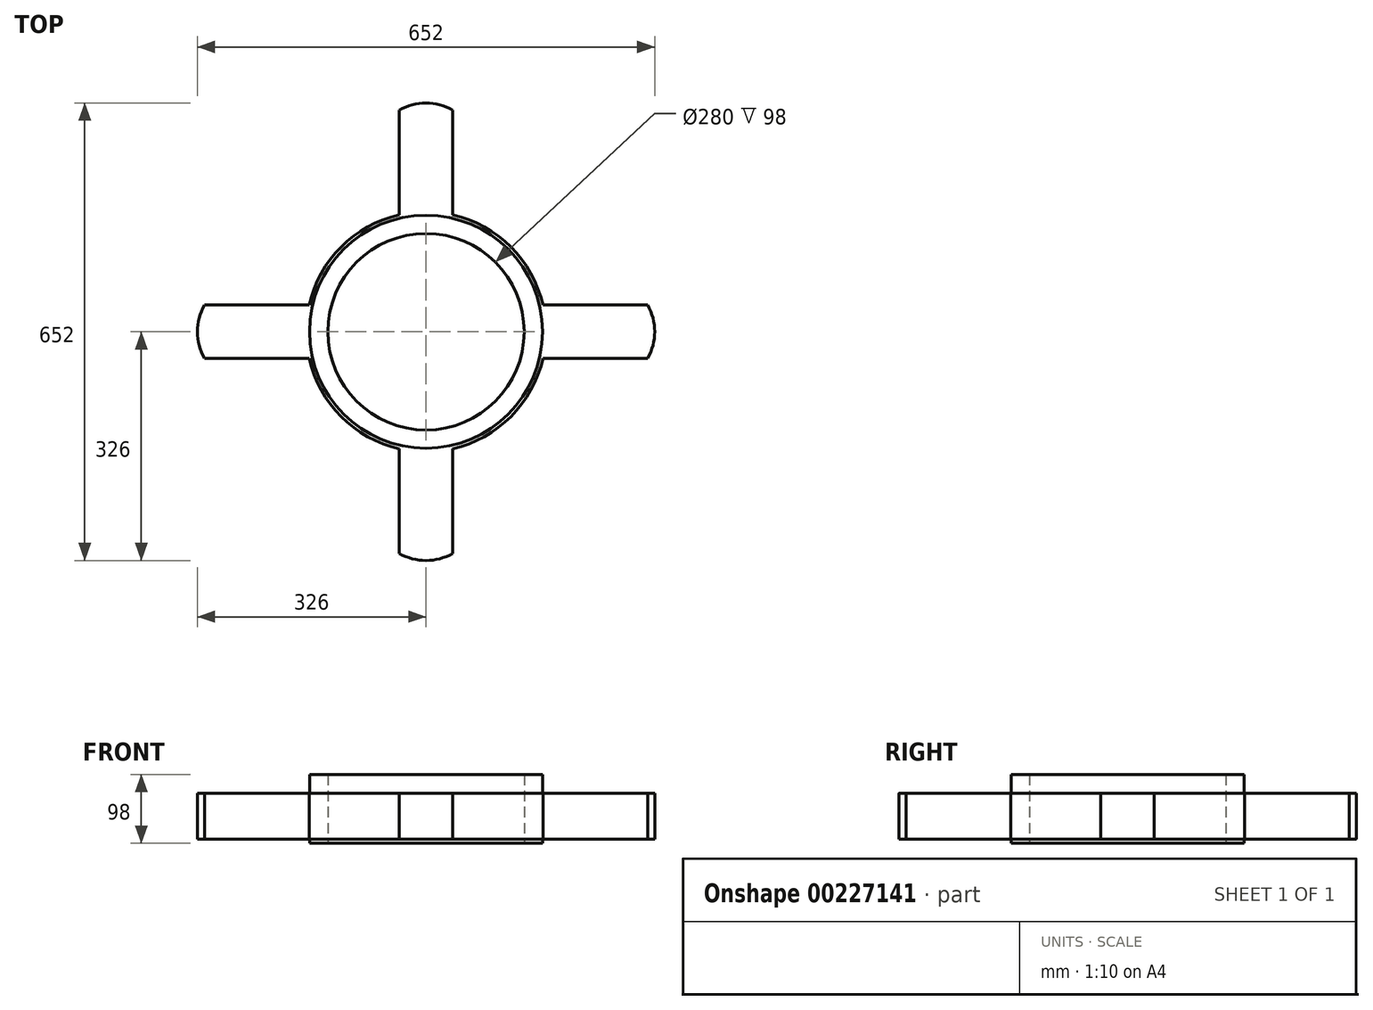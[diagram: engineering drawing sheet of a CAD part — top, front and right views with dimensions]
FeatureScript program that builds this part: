
annotation { "Feature Type Name" : "Feature", "Feature Type Description" : "" }
export const myFeature = defineFeature(function(context is Context, id is Id, definition is map)
    precondition{}
    {
        {
            var Q0;
            Q0=qCreatedBy(makeId("Top.planeOp"),FACE);
            var sketch = newSketch(context, id + "F0", { "sketchPlane" : qUnion([Q0])});
            skCircle(sketch, "E0", {"center": v(0, 0) * mm, "radius": 140 * mm});
            skCircle(sketch, "E1", {"center": v(0, 0) * mm, "radius": 171 * mm});
            skLineSegment(sketch, "E2", {"start": v(0, 171) * mm, "end": v(0, 326) * mm});
            skLineSegment(sketch, "E3", {"start": v(-38, 316) * mm, "end": v(-38, 166.72) * mm});
            skLineSegment(sketch, "E4", {"start": v(38, 316) * mm, "end": v(38, 166.72) * mm});
            skArc(sketch, "E5", {"start": v(38, 316) * mm, "mid": v(0, 326) * mm, "end": v(-38, 316) * mm});
            skLineSegment(sketch, "E6", {"start": v(-171, 0) * mm, "end": v(-326, 0) * mm});
            skLineSegment(sketch, "E7", {"start": v(-316, 38) * mm, "end": v(-166.72, 38) * mm});
            skLineSegment(sketch, "E8", {"start": v(-316, -38) * mm, "end": v(-166.72, -38) * mm});
            skArc(sketch, "E9", {"start": v(-316, 38) * mm, "mid": v(-326, 0) * mm, "end": v(-316, -38) * mm});
            skCircle(sketch, "E10", {"center": v(0, 0) * mm, "radius": 166 * mm});
            skLineSegment(sketch, "E11", {"start": v(0, -171) * mm, "end": v(0, -326) * mm});
            skLineSegment(sketch, "E12", {"start": v(38, -316) * mm, "end": v(38, -166.72) * mm});
            skLineSegment(sketch, "E13", {"start": v(-38, -316) * mm, "end": v(-38, -166.72) * mm});
            skArc(sketch, "E14", {"start": v(-38, -316) * mm, "mid": v(0, -326) * mm, "end": v(38, -316) * mm});
            skLineSegment(sketch, "E15", {"start": v(171, 0) * mm, "end": v(326, 0) * mm});
            skLineSegment(sketch, "E16", {"start": v(316, 38) * mm, "end": v(166.72, 38) * mm});
            skLineSegment(sketch, "E17", {"start": v(316, -38) * mm, "end": v(166.72, -38) * mm});
            skArc(sketch, "E18", {"start": v(316, -38) * mm, "mid": v(326, 0) * mm, "end": v(316, 38) * mm});
            skSolve(sketch);
        }
        {
            var Q0;
            Q0=makeQuery(id+"F0.imprint","IMPRINT",FACE,{"disambiguationData":[TD([[makeQuery(id+"F0.imprint","IMPRINT",EDGE,{"derivedFrom":sQuery(id+"F0.wireOp",EDGE,"E0")}),-1.0]])]});
            extrude(context, id + "F1", {"entities" : qUnion([Q0]), "depth" : 49 * mm});
        }
        {
            var Q0;
            Q0=makeQuery(id+"F0.imprint","IMPRINT",FACE,{"disambiguationData":[TD([[makeQuery(id+"F0.imprint","IMPRINT",EDGE,{"derivedFrom":sQuery(id+"F0.wireOp",EDGE,"E0")}),-1.0]])]});
            extrude(context, id + "F2", {"entities" : qUnion([Q0]), "operationType" : NewBodyOperationType.ADD, "oppositeDirection" : true, "depth" : 49 * mm});
        }
        {
            var Q0;
            Q0=makeQuery(id+"F0.imprint","IMPRINT",FACE,{"disambiguationData":[TD([[makeQuery(id+"F0.imprint","IMPRINT",EDGE,{"derivedFrom":sQuery(id+"F0.wireOp",EDGE,"E10")}),-1.0]])]});
            var Q1;
            {var subQ0=sQuery(id+"F0.wireOp",EDGE,"E6");Q1=makeQuery(id+"F0.imprint","IMPRINT",FACE,{"disambiguationData":[TD([[makeQuery(id+"F0.imprint","IMPRINT",EDGE,{"derivedFrom":subQ0}),1.0]])]});}
            var Q2;
            {var subQ0=sQuery(id+"F0.wireOp",EDGE,"E6");Q2=makeQuery(id+"F0.imprint","IMPRINT",FACE,{"disambiguationData":[TD([[makeQuery(id+"F0.imprint","IMPRINT",EDGE,{"derivedFrom":subQ0}),-1.0]])]});}
            var Q3;
            {var subQ0=sQuery(id+"F0.wireOp",EDGE,"E2");Q3=makeQuery(id+"F0.imprint","IMPRINT",FACE,{"disambiguationData":[TD([[makeQuery(id+"F0.imprint","IMPRINT",EDGE,{"derivedFrom":subQ0}),1.0]])]});}
            var Q4;
            {var subQ0=sQuery(id+"F0.wireOp",EDGE,"E2");Q4=makeQuery(id+"F0.imprint","IMPRINT",FACE,{"disambiguationData":[TD([[makeQuery(id+"F0.imprint","IMPRINT",EDGE,{"derivedFrom":subQ0}),-1.0]])]});}
            var Q5;
            {var subQ0=sQuery(id+"F0.wireOp",EDGE,"E15");Q5=makeQuery(id+"F0.imprint","IMPRINT",FACE,{"disambiguationData":[TD([[makeQuery(id+"F0.imprint","IMPRINT",EDGE,{"derivedFrom":subQ0}),1.0]])]});}
            var Q6;
            {var subQ0=sQuery(id+"F0.wireOp",EDGE,"E15");Q6=makeQuery(id+"F0.imprint","IMPRINT",FACE,{"disambiguationData":[TD([[makeQuery(id+"F0.imprint","IMPRINT",EDGE,{"derivedFrom":subQ0}),-1.0]])]});}
            var Q7;
            {var subQ0=sQuery(id+"F0.wireOp",EDGE,"E11");Q7=makeQuery(id+"F0.imprint","IMPRINT",FACE,{"disambiguationData":[TD([[makeQuery(id+"F0.imprint","IMPRINT",EDGE,{"derivedFrom":subQ0}),1.0]])]});}
            var Q8;
            {var subQ0=sQuery(id+"F0.wireOp",EDGE,"E11");Q8=makeQuery(id+"F0.imprint","IMPRINT",FACE,{"disambiguationData":[TD([[makeQuery(id+"F0.imprint","IMPRINT",EDGE,{"derivedFrom":subQ0}),-1.0]])]});}
            extrude(context, id + "F3", {"entities" : qUnion([Q0, Q1, Q2, Q3, Q4, Q5, Q6, Q7, Q8]), "operationType" : NewBodyOperationType.ADD, "depth" : 22 * mm});
        }
        {
            var Q0;
            {var subQ0=sQuery(id+"F0.wireOp",EDGE,"E6");Q0=makeQuery(id+"F0.imprint","IMPRINT",FACE,{"disambiguationData":[TD([[makeQuery(id+"F0.imprint","IMPRINT",EDGE,{"derivedFrom":subQ0}),-1.0]])]});}
            var Q1;
            {var subQ0=sQuery(id+"F0.wireOp",EDGE,"E6");Q1=makeQuery(id+"F0.imprint","IMPRINT",FACE,{"disambiguationData":[TD([[makeQuery(id+"F0.imprint","IMPRINT",EDGE,{"derivedFrom":subQ0}),1.0]])]});}
            var Q2;
            Q2=makeQuery(id+"F0.imprint","IMPRINT",FACE,{"disambiguationData":[TD([[makeQuery(id+"F0.imprint","IMPRINT",EDGE,{"derivedFrom":sQuery(id+"F0.wireOp",EDGE,"E10")}),-1.0]])]});
            var Q3;
            {var subQ0=sQuery(id+"F0.wireOp",EDGE,"E11");Q3=makeQuery(id+"F0.imprint","IMPRINT",FACE,{"disambiguationData":[TD([[makeQuery(id+"F0.imprint","IMPRINT",EDGE,{"derivedFrom":subQ0}),-1.0]])]});}
            var Q4;
            {var subQ0=sQuery(id+"F0.wireOp",EDGE,"E11");Q4=makeQuery(id+"F0.imprint","IMPRINT",FACE,{"disambiguationData":[TD([[makeQuery(id+"F0.imprint","IMPRINT",EDGE,{"derivedFrom":subQ0}),1.0]])]});}
            var Q5;
            {var subQ0=sQuery(id+"F0.wireOp",EDGE,"E15");Q5=makeQuery(id+"F0.imprint","IMPRINT",FACE,{"disambiguationData":[TD([[makeQuery(id+"F0.imprint","IMPRINT",EDGE,{"derivedFrom":subQ0}),-1.0]])]});}
            var Q6;
            {var subQ0=sQuery(id+"F0.wireOp",EDGE,"E15");Q6=makeQuery(id+"F0.imprint","IMPRINT",FACE,{"disambiguationData":[TD([[makeQuery(id+"F0.imprint","IMPRINT",EDGE,{"derivedFrom":subQ0}),1.0]])]});}
            var Q7;
            {var subQ0=sQuery(id+"F0.wireOp",EDGE,"E2");Q7=makeQuery(id+"F0.imprint","IMPRINT",FACE,{"disambiguationData":[TD([[makeQuery(id+"F0.imprint","IMPRINT",EDGE,{"derivedFrom":subQ0}),-1.0]])]});}
            var Q8;
            {var subQ0=sQuery(id+"F0.wireOp",EDGE,"E2");Q8=makeQuery(id+"F0.imprint","IMPRINT",FACE,{"disambiguationData":[TD([[makeQuery(id+"F0.imprint","IMPRINT",EDGE,{"derivedFrom":subQ0}),1.0]])]});}
            extrude(context, id + "F4", {"entities" : qUnion([Q0, Q1, Q2, Q3, Q4, Q5, Q6, Q7, Q8]), "operationType" : NewBodyOperationType.ADD, "oppositeDirection" : true, "depth" : 43 * mm});
        }
    });
